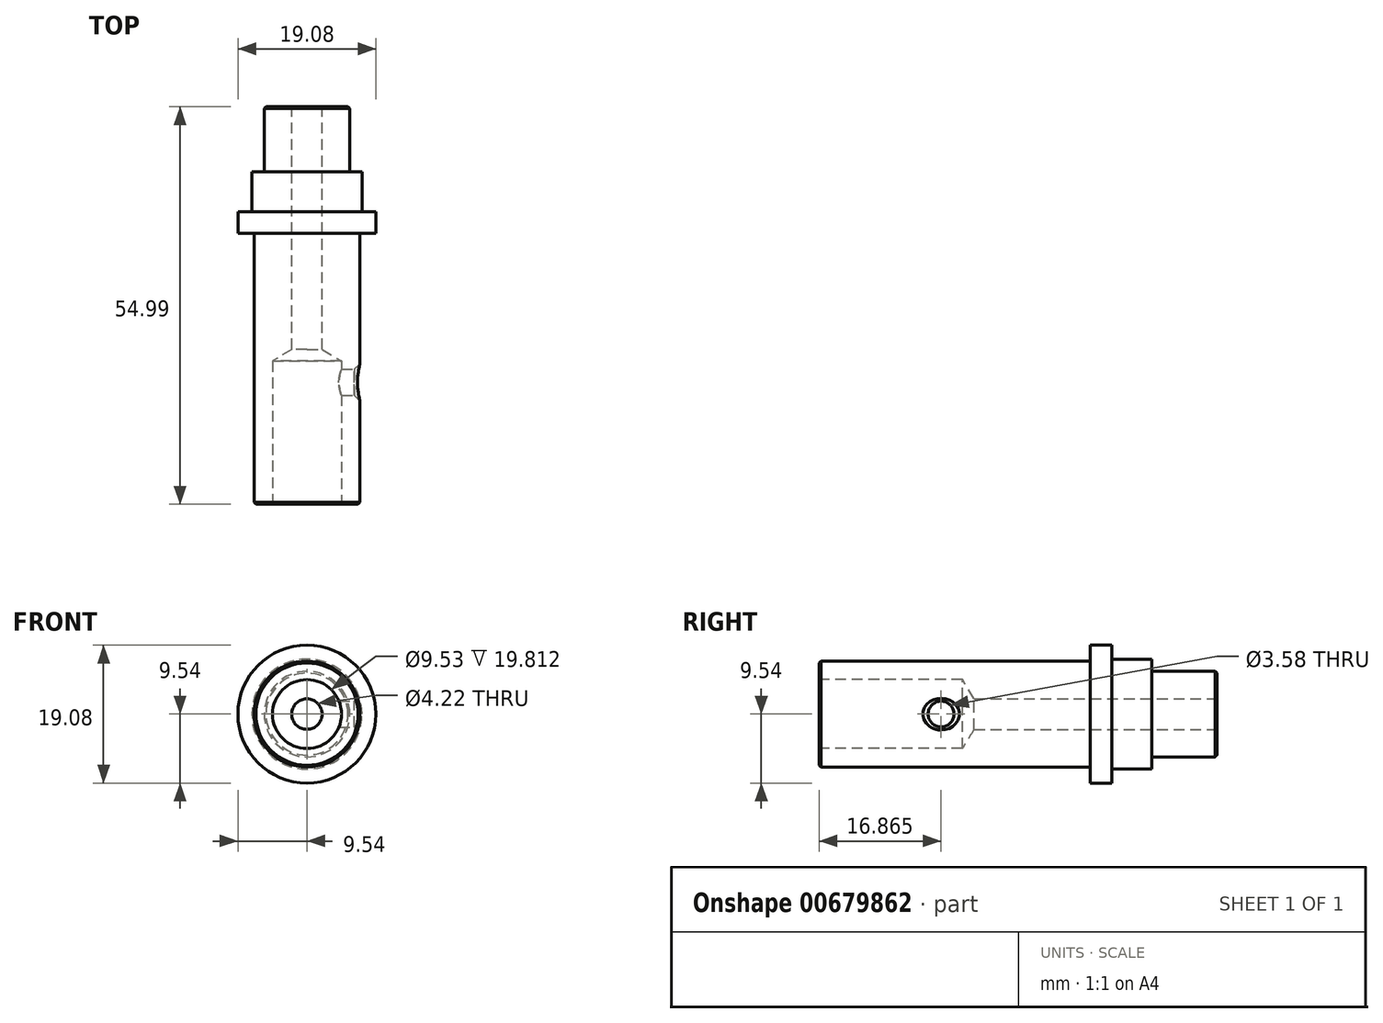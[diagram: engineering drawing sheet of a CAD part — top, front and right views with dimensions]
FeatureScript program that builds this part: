
annotation { "Feature Type Name" : "Feature", "Feature Type Description" : "" }
export const myFeature = defineFeature(function(context is Context, id is Id, definition is map)
    precondition{}
    {
        {
            var Q0;
            Q0=qCreatedBy(makeId("Front.planeOp"),FACE);
            var sketch = newSketch(context, id + "F0", { "sketchPlane" : qUnion([Q0])});
            skCircle(sketch, "E0", {"center": v(0, 0) * mm, "radius": 7.33 * mm});
            skSolve(sketch);
        }
        {
            var Q0;
            Q0=qCreatedBy(makeId("Front.planeOp"),FACE);
            var sketch = newSketch(context, id + "F1", { "sketchPlane" : qUnion([Q0])});
            skCircle(sketch, "E1", {"center": v(0, 0) * mm, "radius": 9.54 * mm});
            skSolve(sketch);
        }
        {
            var Q0;
            Q0=qCreatedBy(makeId("Top.planeOp"),FACE);
            var sketch = newSketch(context, id + "F2", { "sketchPlane" : qUnion([Q0])});
            skSolve(sketch);
        }
        {
            var Q0;
            Q0=qCreatedBy(makeId("Front.planeOp"),FACE);
            var sketch = newSketch(context, id + "F3", { "sketchPlane" : qUnion([Q0])});
            skCircle(sketch, "E2", {"center": v(0, 0) * mm, "radius": 7.6 * mm});
            skSolve(sketch);
        }
        {
            var Q0;
            Q0=qCreatedBy(makeId("Front.planeOp"),FACE);
            var sketch = newSketch(context, id + "F4", { "sketchPlane" : qUnion([Q0])});
            skCircle(sketch, "E3", {"center": v(0, 0) * mm, "radius": 5.92 * mm});
            skSolve(sketch);
        }
        {
            var Q0;
            Q0 = qSketchRegion(id + "F0", true);
            extrude(context, id + "F5", {"entities" : qUnion([Q0]), "depth" : 37.5 * mm, "offsetDistance" : 25.4 * mm});
        }
        {
            var Q0;
            Q0 = qSketchRegion(id + "F1", true);
            var Q1;
            Q1 = qSketchRegion(id + "F2", true);
            extrude(context, id + "F6", {"entities" : qUnion([Q0, Q1]), "operationType" : NewBodyOperationType.ADD, "oppositeDirection" : true, "depth" : 3 * mm, "offsetDistance" : 25.4 * mm});
        }
        {
            var Q0;
            Q0 = qSketchRegion(id + "F3", true);
            extrude(context, id + "F7", {"entities" : qUnion([Q0]), "operationType" : NewBodyOperationType.ADD, "oppositeDirection" : true, "depth" : 8.5 * mm, "offsetDistance" : 25.4 * mm});
        }
        {
            var Q0;
            Q0 = qSketchRegion(id + "F4", true);
            extrude(context, id + "F8", {"entities" : qUnion([Q0]), "operationType" : NewBodyOperationType.ADD, "oppositeDirection" : true, "depth" : 17.5 * mm, "offsetDistance" : 25.4 * mm});
        }
        {
            var Q0;
            Q0=makeQuery(id+"F5.opExtrude","CAP_EDGE",EDGE,{"disambiguationData":[OSD([sQuery(id+"F0.wireOp",EDGE,"E0")])],"isStart":false});
            var Q1;
            Q1=makeQuery(id+"F8.opExtrude","CAP_EDGE",EDGE,{"disambiguationData":[OSD([sQuery(id+"F4.wireOp",EDGE,"E3")])],"isStart":false});
            chamfer(context, id + "F9", {"entities" : qUnion([Q0, Q1]), "width" : 0.25 * mm, "tangentPropagation" : true});
        }
        {
            var Q0;
            Q0=makeQuery(id+"F5.opExtrude","CAP_FACE",FACE,{"disambiguationData":[OSD([sQuery(id+"F0.wireOp",EDGE,"E0")])],"isStart":false});
            var sketch = newSketch(context, id + "F10", { "sketchPlane" : qUnion([Q0])});
            skPoint(sketch, "E4", {"position": v(0, 0) * mm});
            skSolve(sketch);
        }
        {
            var Q0;
            Q0=sQuery(id+"F10.wireOp",VERTEX,"E4");
            var Q1;
            Q1=makeQuery(id+"F5.opExtrude","SWEPT_BODY",BODY,{"disambiguationData":[OSD([sQuery(id+"F0.wireOp",EDGE,"E0")])]});
            hole(context, id + "F11", {"style" : HoleStyle.SIMPLE, "endStyle" : HoleEndStyle.BLIND, "holeDiameter" : 9.52 * mm, "majorDiameter" : 6.35 * mm, "holeDepth" : 19.8 * mm, "isTappedThrough" : true, "tappedDepth" : 12.7 * mm, "tapClearance" : 3, "startFromSketch" : true, "locations" : qUnion([Q0]), "scope" : qUnion([Q1])});
        }
        {
            var Q0;
            Q0=makeQuery(id+"F8.opExtrude","CAP_FACE",FACE,{"disambiguationData":[OSD([sQuery(id+"F4.wireOp",EDGE,"E3")])],"isStart":false});
            var sketch = newSketch(context, id + "F12", { "sketchPlane" : qUnion([Q0])});
            skPoint(sketch, "E5", {"position": v(0, 0) * mm});
            skSolve(sketch);
        }
        {
            var Q0;
            Q0=sQuery(id+"F12.wireOp",VERTEX,"E5");
            var Q1;
            Q1=makeQuery(id+"F5.opExtrude","SWEPT_BODY",BODY,{"disambiguationData":[OSD([sQuery(id+"F0.wireOp",EDGE,"E0")])]});
            hole(context, id + "F13", {"style" : HoleStyle.SIMPLE, "endStyle" : HoleEndStyle.THROUGH, "holeDiameter" : 4.22 * mm, "majorDiameter" : 6.35 * mm, "isTappedThrough" : true, "tappedDepth" : 12.7 * mm, "tapClearance" : 3, "startFromSketch" : true, "locations" : qUnion([Q0]), "scope" : qUnion([Q1])});
        }
        {
            var Q0;
            Q0=qCreatedBy(makeId("Front.planeOp"),FACE);
            var sketch = newSketch(context, id + "F14", { "sketchPlane" : qUnion([Q0])});
            skPoint(sketch, "E6", {"position": v(0, 0) * mm});
            skSolve(sketch);
        }
        {
            var Q0;
            Q0=qCreatedBy(makeId("Right.planeOp"),FACE);
            cPlane(context, id + "F15", {"entities" : qUnion([Q0]), "cplaneType" : CPlaneType.OFFSET, "offset" : 7.33 * mm, "width" : 152.4 * mm, "height" : 152.4 * mm});
        }
        {
            var Q0;
            Q0=qCreatedBy(id+"F15.planeOp",FACE);
            var sketch = newSketch(context, id + "F16", { "sketchPlane" : qUnion([Q0])});
            skPoint(sketch, "E7", {"position": v(-20.62, 0) * mm});
            skSolve(sketch);
        }
        {
            var Q0;
            Q0=sQuery(id+"F16.wireOp",VERTEX,"E7");
            var Q1;
            Q1=makeQuery(id+"F5.opExtrude","SWEPT_BODY",BODY,{"disambiguationData":[OSD([sQuery(id+"F0.wireOp",EDGE,"E0")])]});
            hole(context, id + "F17", {"style" : HoleStyle.C_SINK, "endStyle" : HoleEndStyle.BLIND, "holeDiameter" : 3.58 * mm, "cSinkDiameter" : 5.08 * mm, "cSinkAngle" : 90 * degree, "majorDiameter" : 6.35 * mm, "holeDepth" : 6.35 * mm, "isTappedThrough" : true, "tappedDepth" : 12.7 * mm, "tapClearance" : 3, "startFromSketch" : true, "locations" : qUnion([Q0]), "scope" : qUnion([Q1])});
        }
    });
